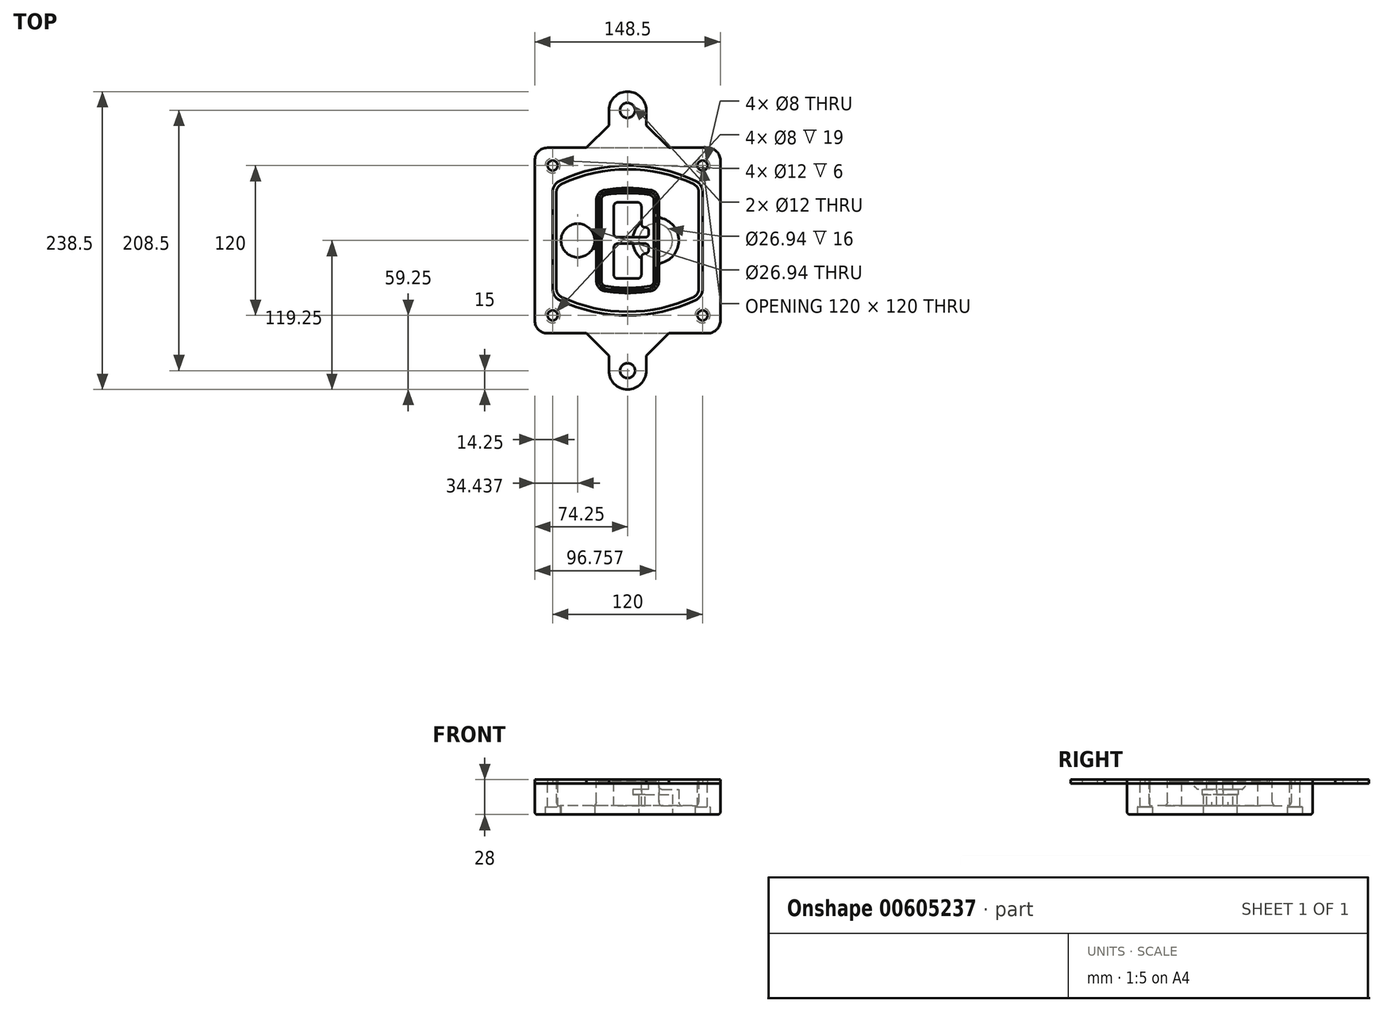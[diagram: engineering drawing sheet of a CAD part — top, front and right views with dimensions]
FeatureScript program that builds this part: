
annotation { "Feature Type Name" : "Feature", "Feature Type Description" : "" }
export const myFeature = defineFeature(function(context is Context, id is Id, definition is map)
    precondition{}
    {
        {
            var Q0;
            Q0=qCreatedBy(makeId("Top.planeOp"),FACE);
            var sketch = newSketch(context, id + "F0", { "sketchPlane" : qUnion([Q0])});
            skPoint(sketch, "E0.rect.middle", {"position": v(0, 0) * mm});
            skLineSegment(sketch, "E1.bottom", {"start": v(-64.25, -74.25) * mm, "end": v(64.25, -74.25) * mm});
            skLineSegment(sketch, "E1.top", {"start": v(-64.25, 74.25) * mm, "end": v(64.25, 74.25) * mm});
            skLineSegment(sketch, "E1.left", {"start": v(-74.25, -64.25) * mm, "end": v(-74.25, 64.25) * mm});
            skLineSegment(sketch, "E1.right", {"start": v(74.25, -64.25) * mm, "end": v(74.25, 64.25) * mm});
            skLineSegment(sketch, "E2", {"start": v(-74.25, 74.25) * mm, "end": v(74.25, -74.25) * mm, "construction": true});
            skLineSegment(sketch, "E3", {"start": v(74.25, 74.25) * mm, "end": v(-74.25, -74.25) * mm, "construction": true});
            skCircle(sketch, "E4", {"center": v(-60, 60) * mm, "radius": 4 * mm});
            skCircle(sketch, "E5", {"center": v(60, 60) * mm, "radius": 4 * mm});
            skCircle(sketch, "E6", {"center": v(60, -60) * mm, "radius": 4 * mm});
            skCircle(sketch, "E7", {"center": v(-60, -60) * mm, "radius": 4 * mm});
            skLineSegment(sketch, "E8", {"start": v(-60, 60) * mm, "end": v(60, 60) * mm, "construction": true});
            skLineSegment(sketch, "E9", {"start": v(60, 60) * mm, "end": v(60, -60) * mm, "construction": true});
            skLineSegment(sketch, "E10", {"start": v(60, -60) * mm, "end": v(-60, -60) * mm, "construction": true});
            skLineSegment(sketch, "E11", {"start": v(-60, -60) * mm, "end": v(-60, 60) * mm, "construction": true});
            skLineSegment(sketch, "E12", {"start": v(-60, 38.83) * mm, "end": v(-60, -38.83) * mm});
            skLineSegment(sketch, "E13", {"start": v(60, 38.83) * mm, "end": v(60, -38.83) * mm});
            skArc(sketch, "E14", {"start": v(54.26, 47.88) * mm, "mid": v(0, 60) * mm, "end": v(-54.26, 47.88) * mm});
            skArc(sketch, "E15", {"start": v(-54.26, -47.88) * mm, "mid": v(0, -60) * mm, "end": v(54.26, -47.88) * mm});
            skLineSegment(sketch, "E16", {"start": v(-60, 0) * mm, "end": v(60, 0) * mm, "construction": true});
            skPoint(sketch, "E17.visualSharp", {"position": v(-60, -45) * mm});
            skArc(sketch, "E17.filletArc", {"start": v(-60, -38.83) * mm, "mid": v(-58.44, -44.2) * mm, "end": v(-54.26, -47.88) * mm});
            skPoint(sketch, "E18.visualSharp", {"position": v(-60, 45) * mm});
            skArc(sketch, "E18.filletArc", {"start": v(-54.26, 47.88) * mm, "mid": v(-58.44, 44.2) * mm, "end": v(-60, 38.83) * mm});
            skPoint(sketch, "E19.visualSharp", {"position": v(60, 45) * mm});
            skArc(sketch, "E19.filletArc", {"start": v(60, 38.83) * mm, "mid": v(58.44, 44.2) * mm, "end": v(54.26, 47.88) * mm});
            skPoint(sketch, "E20.visualSharp", {"position": v(60, -45) * mm});
            skArc(sketch, "E20.filletArc", {"start": v(54.26, -47.88) * mm, "mid": v(58.44, -44.2) * mm, "end": v(60, -38.83) * mm});
            skPoint(sketch, "E21.visualSharp", {"position": v(-74.25, 74.25) * mm});
            skArc(sketch, "E21.filletArc", {"start": v(-64.25, 74.25) * mm, "mid": v(-71.32, 71.32) * mm, "end": v(-74.25, 64.25) * mm});
            skPoint(sketch, "E22.visualSharp", {"position": v(74.25, 74.25) * mm});
            skArc(sketch, "E22.filletArc", {"start": v(74.25, 64.25) * mm, "mid": v(71.32, 71.32) * mm, "end": v(64.25, 74.25) * mm});
            skPoint(sketch, "E23.visualSharp", {"position": v(74.25, -74.25) * mm});
            skArc(sketch, "E23.filletArc", {"start": v(64.25, -74.25) * mm, "mid": v(71.32, -71.32) * mm, "end": v(74.25, -64.25) * mm});
            skPoint(sketch, "E24.visualSharp", {"position": v(-74.25, -74.25) * mm});
            skArc(sketch, "E24.filletArc", {"start": v(-74.25, -64.25) * mm, "mid": v(-71.32, -71.32) * mm, "end": v(-64.25, -74.25) * mm});
            skArc(sketch, "E25.0", {"start": v(57, 38.83) * mm, "mid": v(55.9, 42.58) * mm, "end": v(52.98, 45.17) * mm});
            skLineSegment(sketch, "E25.1", {"start": v(57, 38.83) * mm, "end": v(57, -38.83) * mm});
            skArc(sketch, "E25.2", {"start": v(52.98, -45.17) * mm, "mid": v(55.9, -42.58) * mm, "end": v(57, -38.83) * mm});
            skArc(sketch, "E25.3", {"start": v(-52.98, -45.17) * mm, "mid": v(0, -57) * mm, "end": v(52.98, -45.17) * mm});
            skArc(sketch, "E25.4", {"start": v(-57, -38.83) * mm, "mid": v(-55.9, -42.58) * mm, "end": v(-52.98, -45.17) * mm});
            skArc(sketch, "E25.5", {"start": v(52.98, 45.17) * mm, "mid": v(0, 57) * mm, "end": v(-52.98, 45.17) * mm});
            skLineSegment(sketch, "E25.6", {"start": v(-57, 38.83) * mm, "end": v(-57, -38.83) * mm});
            skArc(sketch, "E25.7", {"start": v(-52.98, 45.17) * mm, "mid": v(-55.9, 42.58) * mm, "end": v(-57, 38.83) * mm});
            skArc(sketch, "E26.0", {"start": v(-55.96, 51.5) * mm, "mid": v(-61.82, 46.33) * mm, "end": v(-64, 38.83) * mm});
            skArc(sketch, "E26.1", {"start": v(55.96, 51.5) * mm, "mid": v(0, 64) * mm, "end": v(-55.96, 51.5) * mm});
            skArc(sketch, "E26.2", {"start": v(64, 38.83) * mm, "mid": v(61.82, 46.33) * mm, "end": v(55.96, 51.5) * mm});
            skLineSegment(sketch, "E26.3", {"start": v(64, 38.83) * mm, "end": v(64, -38.83) * mm});
            skArc(sketch, "E26.4", {"start": v(55.96, -51.5) * mm, "mid": v(61.82, -46.33) * mm, "end": v(64, -38.83) * mm});
            skLineSegment(sketch, "E26.5", {"start": v(-64, 38.83) * mm, "end": v(-64, -38.83) * mm});
            skArc(sketch, "E26.6", {"start": v(-55.96, -51.5) * mm, "mid": v(0, -64) * mm, "end": v(55.96, -51.5) * mm});
            skArc(sketch, "E26.7", {"start": v(-64, -38.83) * mm, "mid": v(-61.82, -46.33) * mm, "end": v(-55.96, -51.5) * mm});
            skSolve(sketch);
        }
        {
            var Q0;
            Q0=makeQuery(id+"F0.imprint","IMPRINT",FACE,{"disambiguationData":[TD([[makeQuery(id+"F0.imprint","IMPRINT",EDGE,{"derivedFrom":sQuery(id+"F0.wireOp",EDGE,"E1.bottom")}),1.0]])]});
            var Q1;
            Q1=makeQuery(id+"F0.imprint","IMPRINT",FACE,{"disambiguationData":[TD([[makeQuery(id+"F0.imprint","IMPRINT",EDGE,{"derivedFrom":sQuery(id+"F0.wireOp",EDGE,"E12")}),1.0]])]});
            var Q2;
            Q2=makeQuery(id+"F0.imprint","IMPRINT",FACE,{"disambiguationData":[TD([[makeQuery(id+"F0.imprint","IMPRINT",EDGE,{"derivedFrom":sQuery(id+"F0.wireOp",EDGE,"E25.0")}),1.0]])]});
            var Q3;
            Q3=makeQuery(id+"F0.imprint","IMPRINT",FACE,{"disambiguationData":[TD([[makeQuery(id+"F0.imprint","IMPRINT",EDGE,{"derivedFrom":sQuery(id+"F0.wireOp",EDGE,"E12")}),-1.0]])]});
            extrude(context, id + "F1", {"entities" : qUnion([Q0, Q1, Q2, Q3]), "oppositeDirection" : true, "depth" : 25 * mm});
        }
        {
            var Q0;
            Q0=makeQuery(id+"F0.imprint","IMPRINT",FACE,{"disambiguationData":[TD([[makeQuery(id+"F0.imprint","IMPRINT",EDGE,{"derivedFrom":sQuery(id+"F0.wireOp",EDGE,"E12")}),1.0]])]});
            extrude(context, id + "F2", {"entities" : qUnion([Q0]), "operationType" : NewBodyOperationType.ADD, "depth" : 3 * mm});
        }
        {
            var Q0;
            Q0=makeQuery(id+"F0.imprint","IMPRINT",FACE,{"disambiguationData":[TD([[makeQuery(id+"F0.imprint","IMPRINT",EDGE,{"derivedFrom":sQuery(id+"F0.wireOp",EDGE,"E25.0")}),1.0]])]});
            extrude(context, id + "F3", {"entities" : qUnion([Q0]), "operationType" : NewBodyOperationType.REMOVE, "oppositeDirection" : true, "depth" : 18 * mm});
        }
        {
            var Q0;
            Q0=makeQuery(id+"F2.opExtrude","CAP_FACE",FACE,{"disambiguationData":[OSD([sQuery(id+"F0.wireOp",EDGE,"E12"),sQuery(id+"F0.wireOp",EDGE,"E13"),sQuery(id+"F0.wireOp",EDGE,"E14"),sQuery(id+"F0.wireOp",EDGE,"E15"),sQuery(id+"F0.wireOp",EDGE,"E17.filletArc"),sQuery(id+"F0.wireOp",EDGE,"E18.filletArc"),sQuery(id+"F0.wireOp",EDGE,"E19.filletArc"),sQuery(id+"F0.wireOp",EDGE,"E20.filletArc"),sQuery(id+"F0.wireOp",EDGE,"E25.0"),sQuery(id+"F0.wireOp",EDGE,"E25.1"),sQuery(id+"F0.wireOp",EDGE,"E25.2"),sQuery(id+"F0.wireOp",EDGE,"E25.3"),sQuery(id+"F0.wireOp",EDGE,"E25.4"),sQuery(id+"F0.wireOp",EDGE,"E25.5"),sQuery(id+"F0.wireOp",EDGE,"E25.6"),sQuery(id+"F0.wireOp",EDGE,"E25.7")])],"isStart":false});
            var sketch = newSketch(context, id + "F4", { "sketchPlane" : qUnion([Q0])});
            skArc(sketch, "E27.0", {"start": v(-18.34, -40.45) * mm, "mid": v(0, -42) * mm, "end": v(18.34, -40.45) * mm});
            skArc(sketch, "E28.0", {"start": v(18.34, 40.45) * mm, "mid": v(0, 42) * mm, "end": v(-18.34, 40.45) * mm});
            skLineSegment(sketch, "E29", {"start": v(-25, 32.57) * mm, "end": v(-25, -32.57) * mm});
            skLineSegment(sketch, "E30", {"start": v(25, 32.57) * mm, "end": v(25, -32.57) * mm});
            skLineSegment(sketch, "E31", {"start": v(-25, 39.1) * mm, "end": v(25, 39.1) * mm, "construction": true});
            skLineSegment(sketch, "E32", {"start": v(-25, -39.1) * mm, "end": v(25, -39.1) * mm, "construction": true});
            skPoint(sketch, "E33.visualSharp", {"position": v(-25, 39.1) * mm});
            skArc(sketch, "E33.filletArc", {"start": v(-18.34, 40.45) * mm, "mid": v(-23.11, 37.73) * mm, "end": v(-25, 32.57) * mm});
            skPoint(sketch, "E34.visualSharp", {"position": v(25, 39.1) * mm});
            skArc(sketch, "E34.filletArc", {"start": v(25, 32.57) * mm, "mid": v(23.11, 37.73) * mm, "end": v(18.34, 40.45) * mm});
            skPoint(sketch, "E35.visualSharp", {"position": v(25, -39.1) * mm});
            skArc(sketch, "E35.filletArc", {"start": v(18.34, -40.45) * mm, "mid": v(23.11, -37.73) * mm, "end": v(25, -32.57) * mm});
            skPoint(sketch, "E36.visualSharp", {"position": v(-25, -39.1) * mm});
            skArc(sketch, "E36.filletArc", {"start": v(-25, -32.57) * mm, "mid": v(-23.11, -37.73) * mm, "end": v(-18.34, -40.45) * mm});
            skArc(sketch, "E37.0", {"start": v(52.98, 45.17) * mm, "mid": v(0, 57) * mm, "end": v(-52.98, 45.17) * mm});
            skArc(sketch, "E37.1", {"start": v(-52.98, 45.17) * mm, "mid": v(-55.9, 42.58) * mm, "end": v(-57, 38.83) * mm});
            skLineSegment(sketch, "E37.2", {"start": v(-57, 38.83) * mm, "end": v(-57, -38.83) * mm});
            skArc(sketch, "E37.3", {"start": v(-57, -38.83) * mm, "mid": v(-55.9, -42.58) * mm, "end": v(-52.98, -45.17) * mm});
            skArc(sketch, "E37.4", {"start": v(-52.98, -45.17) * mm, "mid": v(0, -57) * mm, "end": v(52.98, -45.17) * mm});
            skArc(sketch, "E37.5", {"start": v(52.98, -45.17) * mm, "mid": v(55.9, -42.58) * mm, "end": v(57, -38.83) * mm});
            skLineSegment(sketch, "E37.6", {"start": v(57, 38.83) * mm, "end": v(57, -38.83) * mm});
            skArc(sketch, "E37.7", {"start": v(57, 38.83) * mm, "mid": v(55.9, 42.58) * mm, "end": v(52.98, 45.17) * mm});
            skLineSegment(sketch, "E38.0", {"start": v(23, 32.57) * mm, "end": v(23, -32.57) * mm});
            skArc(sketch, "E38.1", {"start": v(18, -38.48) * mm, "mid": v(21.58, -36.44) * mm, "end": v(23, -32.57) * mm});
            skArc(sketch, "E38.2", {"start": v(-18, -38.48) * mm, "mid": v(0, -40) * mm, "end": v(18, -38.48) * mm});
            skArc(sketch, "E38.3", {"start": v(-23, -32.57) * mm, "mid": v(-21.58, -36.44) * mm, "end": v(-18, -38.48) * mm});
            skLineSegment(sketch, "E38.4", {"start": v(-23, 32.57) * mm, "end": v(-23, -32.57) * mm});
            skArc(sketch, "E38.5", {"start": v(23, 32.57) * mm, "mid": v(21.58, 36.44) * mm, "end": v(18, 38.48) * mm});
            skArc(sketch, "E38.6", {"start": v(-18, 38.48) * mm, "mid": v(-21.58, 36.44) * mm, "end": v(-23, 32.57) * mm});
            skArc(sketch, "E38.7", {"start": v(18, 38.48) * mm, "mid": v(0, 40) * mm, "end": v(-18, 38.48) * mm});
            skArc(sketch, "E39.0", {"start": v(21, 32.57) * mm, "mid": v(20.06, 35.15) * mm, "end": v(17.67, 36.5) * mm});
            skLineSegment(sketch, "E39.1", {"start": v(21, 32.57) * mm, "end": v(21, -32.57) * mm});
            skArc(sketch, "E39.2", {"start": v(17.67, -36.5) * mm, "mid": v(20.06, -35.15) * mm, "end": v(21, -32.57) * mm});
            skArc(sketch, "E39.3", {"start": v(-17.67, -36.5) * mm, "mid": v(0, -38) * mm, "end": v(17.67, -36.5) * mm});
            skArc(sketch, "E39.4", {"start": v(-21, -32.57) * mm, "mid": v(-20.06, -35.15) * mm, "end": v(-17.67, -36.5) * mm});
            skArc(sketch, "E39.5", {"start": v(17.67, 36.5) * mm, "mid": v(0, 38) * mm, "end": v(-17.67, 36.5) * mm});
            skLineSegment(sketch, "E39.6", {"start": v(-21, 32.57) * mm, "end": v(-21, -32.57) * mm});
            skArc(sketch, "E39.7", {"start": v(-17.67, 36.5) * mm, "mid": v(-20.06, 35.15) * mm, "end": v(-21, 32.57) * mm});
            skLineSegment(sketch, "E40", {"start": v(-25, 0) * mm, "end": v(25, 0) * mm, "construction": true});
            skLineSegment(sketch, "E41", {"start": v(-11, 5.5) * mm, "end": v(-11, 27.5) * mm});
            skLineSegment(sketch, "E42", {"start": v(-8, 30.5) * mm, "end": v(8, 30.5) * mm});
            skLineSegment(sketch, "E43", {"start": v(11, 27.5) * mm, "end": v(11, 13.5) * mm});
            skLineSegment(sketch, "E44", {"start": v(14, 10.5) * mm, "end": v(14, 10.5) * mm});
            skLineSegment(sketch, "E45", {"start": v(17, 7.5) * mm, "end": v(17, 5.5) * mm});
            skLineSegment(sketch, "E46", {"start": v(14, 2.5) * mm, "end": v(-8, 2.5) * mm});
            skPoint(sketch, "E47.visualSharp", {"position": v(-11, 30.5) * mm});
            skArc(sketch, "E47.filletArc", {"start": v(-8, 30.5) * mm, "mid": v(-10.12, 29.62) * mm, "end": v(-11, 27.5) * mm});
            skPoint(sketch, "E48.visualSharp", {"position": v(11, 30.5) * mm});
            skArc(sketch, "E48.filletArc", {"start": v(11, 27.5) * mm, "mid": v(10.12, 29.62) * mm, "end": v(8, 30.5) * mm});
            skPoint(sketch, "E49.visualSharp", {"position": v(11, 10.5) * mm});
            skArc(sketch, "E49.filletArc", {"start": v(11, 13.5) * mm, "mid": v(11.88, 11.38) * mm, "end": v(14, 10.5) * mm});
            skPoint(sketch, "E50.visualSharp", {"position": v(17, 10.5) * mm});
            skArc(sketch, "E50.filletArc", {"start": v(17, 7.5) * mm, "mid": v(16.12, 9.62) * mm, "end": v(14, 10.5) * mm});
            skPoint(sketch, "E51.visualSharp", {"position": v(17, 2.5) * mm});
            skArc(sketch, "E51.filletArc", {"start": v(14, 2.5) * mm, "mid": v(16.12, 3.38) * mm, "end": v(17, 5.5) * mm});
            skPoint(sketch, "E52.visualSharp", {"position": v(-11, 2.5) * mm});
            skArc(sketch, "E52.filletArc", {"start": v(-11, 5.5) * mm, "mid": v(-10.12, 3.38) * mm, "end": v(-8, 2.5) * mm});
            skLineSegment(sketch, "E53.0.MirrorCS", {"start": v(14, -2.5) * mm, "end": v(-8, -2.5) * mm});
            skArc(sketch, "E54.0.MirrorCS", {"start": v(-11, -5.5) * mm, "mid": v(-10.12, -3.38) * mm, "end": v(-8, -2.5) * mm});
            skLineSegment(sketch, "E55.0.MirrorCS", {"start": v(-11, -5.5) * mm, "end": v(-11, -27.5) * mm});
            skArc(sketch, "E56.0.MirrorCS", {"start": v(-8, -30.5) * mm, "mid": v(-10.12, -29.62) * mm, "end": v(-11, -27.5) * mm});
            skLineSegment(sketch, "E57.0.MirrorCS", {"start": v(-8, -30.5) * mm, "end": v(8, -30.5) * mm});
            skArc(sketch, "E58.0.MirrorCS", {"start": v(11, -27.5) * mm, "mid": v(10.12, -29.62) * mm, "end": v(8, -30.5) * mm});
            skLineSegment(sketch, "E59.0.MirrorCS", {"start": v(11, -27.5) * mm, "end": v(11, -13.5) * mm});
            skArc(sketch, "E60.0.MirrorCS", {"start": v(11, -13.5) * mm, "mid": v(11.88, -11.38) * mm, "end": v(14, -10.5) * mm});
            skArc(sketch, "E61.0.MirrorCS", {"start": v(17, -7.5) * mm, "mid": v(16.12, -9.62) * mm, "end": v(14, -10.5) * mm});
            skLineSegment(sketch, "E62.0.MirrorCS", {"start": v(17, -7.5) * mm, "end": v(17, -5.5) * mm});
            skArc(sketch, "E63.0.MirrorCS", {"start": v(14, -2.5) * mm, "mid": v(16.12, -3.38) * mm, "end": v(17, -5.5) * mm});
            skSolve(sketch);
        }
        {
            var Q0;
            Q0=makeQuery(id+"F4.imprint","IMPRINT",FACE,{"disambiguationData":[TD([[makeQuery(id+"F4.imprint","IMPRINT",EDGE,{"derivedFrom":sQuery(id+"F4.wireOp",EDGE,"E27.0")}),1.0]])]});
            var Q1;
            Q1=makeQuery(id+"F4.imprint","IMPRINT",FACE,{"disambiguationData":[TD([[makeQuery(id+"F4.imprint","IMPRINT",EDGE,{"derivedFrom":sQuery(id+"F4.wireOp",EDGE,"E38.0")}),-1.0]])]});
            var Q2;
            Q2=makeQuery(id+"F4.imprint","IMPRINT",FACE,{"disambiguationData":[TD([[makeQuery(id+"F4.imprint","IMPRINT",EDGE,{"derivedFrom":sQuery(id+"F4.wireOp",EDGE,"E39.0")}),1.0]])]});
            extrude(context, id + "F5", {"entities" : qUnion([Q0, Q1, Q2]), "operationType" : NewBodyOperationType.ADD, "endBound" : BoundingType.UP_TO_NEXT, "oppositeDirection" : true, "depth" : 25 * mm});
        }
        {
            var Q0;
            Q0=makeQuery(id+"F4.imprint","IMPRINT",FACE,{"disambiguationData":[TD([[makeQuery(id+"F4.imprint","IMPRINT",EDGE,{"derivedFrom":sQuery(id+"F4.wireOp",EDGE,"E38.0")}),-1.0]])]});
            extrude(context, id + "F6", {"entities" : qUnion([Q0]), "operationType" : NewBodyOperationType.REMOVE, "oppositeDirection" : true, "depth" : 2 * mm});
        }
        {
            var Q0;
            Q0=makeQuery(id+"F1.opExtrude","CAP_FACE",FACE,{"disambiguationData":[OSD([sQuery(id+"F0.wireOp",EDGE,"E1.bottom"),sQuery(id+"F0.wireOp",EDGE,"E1.top"),sQuery(id+"F0.wireOp",EDGE,"E1.left"),sQuery(id+"F0.wireOp",EDGE,"E1.right"),sQuery(id+"F0.wireOp",EDGE,"E4"),sQuery(id+"F0.wireOp",EDGE,"E5"),sQuery(id+"F0.wireOp",EDGE,"E6"),sQuery(id+"F0.wireOp",EDGE,"E7"),sQuery(id+"F0.wireOp",EDGE,"E21.filletArc"),sQuery(id+"F0.wireOp",EDGE,"E22.filletArc"),sQuery(id+"F0.wireOp",EDGE,"E23.filletArc"),sQuery(id+"F0.wireOp",EDGE,"E24.filletArc")])],"isStart":false});
            var sketch = newSketch(context, id + "F7", { "sketchPlane" : qUnion([Q0])});
            skCircle(sketch, "E64", {"center": v(22.5, 0) * mm, "radius": 13.47 * mm});
            skCircle(sketch, "E65", {"center": v(-39.81, 0) * mm, "radius": 13.47 * mm});
            skLineSegment(sketch, "E66", {"start": v(74.25, 0) * mm, "end": v(-74.25, 0) * mm});
            skCircle(sketch, "E67", {"center": v(22.5, 0) * mm, "radius": 18.47 * mm});
            skCircle(sketch, "E68", {"center": v(60, -60) * mm, "radius": 6 * mm});
            skCircle(sketch, "E69", {"center": v(-60, -60) * mm, "radius": 6 * mm});
            skCircle(sketch, "E70", {"center": v(-60, 60) * mm, "radius": 6 * mm});
            skCircle(sketch, "E71", {"center": v(60, 60) * mm, "radius": 6 * mm});
            skSolve(sketch);
        }
        {
            var Q0;
            {var subQ1=sQuery(id+"F7.wireOp",EDGE,"E66");var subQ4=sQuery(id+"F7.wireOp",EDGE,"E64");var subQ6=makeQuery(id+"F7.imprint","INTERSECT",VERTEX,{"disambiguationData":[OD(0.0)],"derivedFrom":[subQ4,subQ1]});Q0=makeQuery(id+"F7.imprint","IMPRINT",FACE,{"disambiguationData":[TD([[makeQuery(id+"F7.imprint","IMPRINT",EDGE,{"disambiguationData":[TD([[subQ6,-1.0]])],"derivedFrom":subQ4}),-1.0]])]});}
            var Q1;
            {var subQ0=sQuery(id+"F7.wireOp",EDGE,"E66");var subQ1=sQuery(id+"F7.wireOp",EDGE,"E64");var subQ3=makeQuery(id+"F7.imprint","INTERSECT",VERTEX,{"disambiguationData":[OD(0.0)],"derivedFrom":[subQ1,subQ0]});Q1=makeQuery(id+"F7.imprint","IMPRINT",FACE,{"disambiguationData":[TD([[makeQuery(id+"F7.imprint","IMPRINT",EDGE,{"disambiguationData":[TD([[subQ3,-1.0]])],"derivedFrom":subQ1}),1.0]])]});}
            var Q2;
            {var subQ0=sQuery(id+"F7.wireOp",EDGE,"E66");var subQ1=sQuery(id+"F7.wireOp",EDGE,"E64");var subQ3=makeQuery(id+"F7.imprint","INTERSECT",VERTEX,{"disambiguationData":[OD(0.0)],"derivedFrom":[subQ1,subQ0]});Q2=makeQuery(id+"F7.imprint","IMPRINT",FACE,{"disambiguationData":[TD([[makeQuery(id+"F7.imprint","IMPRINT",EDGE,{"disambiguationData":[TD([[subQ3,1.0]])],"derivedFrom":subQ1}),1.0]])]});}
            var Q3;
            {var subQ1=sQuery(id+"F7.wireOp",EDGE,"E66");var subQ4=sQuery(id+"F7.wireOp",EDGE,"E64");var subQ6=makeQuery(id+"F7.imprint","INTERSECT",VERTEX,{"disambiguationData":[OD(0.0)],"derivedFrom":[subQ4,subQ1]});Q3=makeQuery(id+"F7.imprint","IMPRINT",FACE,{"disambiguationData":[TD([[makeQuery(id+"F7.imprint","IMPRINT",EDGE,{"disambiguationData":[TD([[subQ6,1.0]])],"derivedFrom":subQ4}),-1.0]])]});}
            extrude(context, id + "F8", {"entities" : qUnion([Q0, Q1, Q2, Q3]), "operationType" : NewBodyOperationType.ADD, "oppositeDirection" : true, "depth" : 20 * mm});
        }
        {
            var Q0;
            {var subQ0=sQuery(id+"F7.wireOp",EDGE,"E66");var subQ1=sQuery(id+"F7.wireOp",EDGE,"E64");var subQ3=makeQuery(id+"F7.imprint","INTERSECT",VERTEX,{"disambiguationData":[OD(0.0)],"derivedFrom":[subQ1,subQ0]});Q0=makeQuery(id+"F7.imprint","IMPRINT",FACE,{"disambiguationData":[TD([[makeQuery(id+"F7.imprint","IMPRINT",EDGE,{"disambiguationData":[TD([[subQ3,-1.0]])],"derivedFrom":subQ1}),1.0]])]});}
            var Q1;
            {var subQ0=sQuery(id+"F7.wireOp",EDGE,"E66");var subQ1=sQuery(id+"F7.wireOp",EDGE,"E64");var subQ3=makeQuery(id+"F7.imprint","INTERSECT",VERTEX,{"disambiguationData":[OD(0.0)],"derivedFrom":[subQ1,subQ0]});Q1=makeQuery(id+"F7.imprint","IMPRINT",FACE,{"disambiguationData":[TD([[makeQuery(id+"F7.imprint","IMPRINT",EDGE,{"disambiguationData":[TD([[subQ3,1.0]])],"derivedFrom":subQ1}),1.0]])]});}
            extrude(context, id + "F9", {"entities" : qUnion([Q0, Q1]), "operationType" : NewBodyOperationType.REMOVE, "oppositeDirection" : true, "depth" : 16 * mm});
        }
        {
            var Q0;
            {var subQ0=sQuery(id+"F7.wireOp",EDGE,"E66");var subQ1=sQuery(id+"F7.wireOp",EDGE,"E65");var subQ3=makeQuery(id+"F7.imprint","INTERSECT",VERTEX,{"disambiguationData":[OD(0.0)],"derivedFrom":[subQ1,subQ0]});Q0=makeQuery(id+"F7.imprint","IMPRINT",FACE,{"disambiguationData":[TD([[makeQuery(id+"F7.imprint","IMPRINT",EDGE,{"disambiguationData":[TD([[subQ3,-1.0]])],"derivedFrom":subQ1}),1.0]])]});}
            var Q1;
            {var subQ0=sQuery(id+"F7.wireOp",EDGE,"E66");var subQ1=sQuery(id+"F7.wireOp",EDGE,"E65");var subQ3=makeQuery(id+"F7.imprint","INTERSECT",VERTEX,{"disambiguationData":[OD(0.0)],"derivedFrom":[subQ1,subQ0]});Q1=makeQuery(id+"F7.imprint","IMPRINT",FACE,{"disambiguationData":[TD([[makeQuery(id+"F7.imprint","IMPRINT",EDGE,{"disambiguationData":[TD([[subQ3,1.0]])],"derivedFrom":subQ1}),1.0]])]});}
            extrude(context, id + "F10", {"entities" : qUnion([Q0, Q1]), "operationType" : NewBodyOperationType.REMOVE, "oppositeDirection" : true, "depth" : 25 * mm});
        }
        {
            var Q0;
            Q0=makeQuery(id+"F7.imprint","IMPRINT",FACE,{"disambiguationData":[TD([[makeQuery(id+"F7.imprint","IMPRINT",EDGE,{"derivedFrom":sQuery(id+"F7.wireOp",EDGE,"E68")}),1.0]])]});
            var Q1;
            Q1=makeQuery(id+"F7.imprint","IMPRINT",FACE,{"disambiguationData":[TD([[makeQuery(id+"F7.imprint","IMPRINT",EDGE,{"derivedFrom":makeQuery(id+"F1.opExtrude","CAP_EDGE",EDGE,{"disambiguationData":[OSD([sQuery(id+"F0.wireOp",EDGE,"E5")])],"isStart":false})}),-1.0]])]});
            var Q2;
            Q2=makeQuery(id+"F7.imprint","IMPRINT",FACE,{"disambiguationData":[TD([[makeQuery(id+"F7.imprint","IMPRINT",EDGE,{"derivedFrom":sQuery(id+"F7.wireOp",EDGE,"E69")}),1.0]])]});
            var Q3;
            Q3=makeQuery(id+"F7.imprint","IMPRINT",FACE,{"disambiguationData":[TD([[makeQuery(id+"F7.imprint","IMPRINT",EDGE,{"derivedFrom":makeQuery(id+"F1.opExtrude","CAP_EDGE",EDGE,{"disambiguationData":[OSD([sQuery(id+"F0.wireOp",EDGE,"E4")])],"isStart":false})}),-1.0]])]});
            var Q4;
            Q4=makeQuery(id+"F7.imprint","IMPRINT",FACE,{"disambiguationData":[TD([[makeQuery(id+"F7.imprint","IMPRINT",EDGE,{"derivedFrom":sQuery(id+"F7.wireOp",EDGE,"E70")}),1.0]])]});
            var Q5;
            Q5=makeQuery(id+"F7.imprint","IMPRINT",FACE,{"disambiguationData":[TD([[makeQuery(id+"F7.imprint","IMPRINT",EDGE,{"derivedFrom":makeQuery(id+"F1.opExtrude","CAP_EDGE",EDGE,{"disambiguationData":[OSD([sQuery(id+"F0.wireOp",EDGE,"E7")])],"isStart":false})}),-1.0]])]});
            var Q6;
            Q6=makeQuery(id+"F7.imprint","IMPRINT",FACE,{"disambiguationData":[TD([[makeQuery(id+"F7.imprint","IMPRINT",EDGE,{"derivedFrom":sQuery(id+"F7.wireOp",EDGE,"E71")}),1.0]])]});
            var Q7;
            Q7=makeQuery(id+"F7.imprint","IMPRINT",FACE,{"disambiguationData":[TD([[makeQuery(id+"F7.imprint","IMPRINT",EDGE,{"derivedFrom":makeQuery(id+"F1.opExtrude","CAP_EDGE",EDGE,{"disambiguationData":[OSD([sQuery(id+"F0.wireOp",EDGE,"E6")])],"isStart":false})}),-1.0]])]});
            extrude(context, id + "F11", {"entities" : qUnion([Q0, Q1, Q2, Q3, Q4, Q5, Q6, Q7]), "operationType" : NewBodyOperationType.REMOVE, "oppositeDirection" : true, "depth" : 6 * mm});
        }
        {
            var Q0;
            Q0=makeQuery(id+"F9.boolean.opBoolean","COPY",FACE,{"derivedFrom":makeQuery(id+"F9.opExtrude","CAP_FACE",FACE,{"disambiguationData":[OSD([sQuery(id+"F7.wireOp",EDGE,"E64")])],"isStart":false})});
            var sketch = newSketch(context, id + "F12", { "sketchPlane" : qUnion([Q0])});
            skArc(sketch, "E72.0", {"start": v(11, 14.45) * mm, "mid": v(6.45, 9.13) * mm, "end": v(4.2, 2.5) * mm});
            skArc(sketch, "E72.1", {"start": v(4.2, -2.5) * mm, "mid": v(6.45, -9.13) * mm, "end": v(11, -14.45) * mm});
            skLineSegment(sketch, "E73", {"start": v(4.2, -2.5) * mm, "end": v(14, -2.5) * mm});
            skLineSegment(sketch, "E74.0", {"start": v(14, 2.5) * mm, "end": v(4.2, 2.5) * mm});
            skArc(sketch, "E74.1", {"start": v(14, 2.5) * mm, "mid": v(16.12, 3.38) * mm, "end": v(17, 5.5) * mm});
            skLineSegment(sketch, "E74.2", {"start": v(17, 7.5) * mm, "end": v(17, 5.5) * mm});
            skArc(sketch, "E74.3", {"start": v(17, 7.5) * mm, "mid": v(16.12, 9.62) * mm, "end": v(14, 10.5) * mm});
            skArc(sketch, "E74.4", {"start": v(11, 13.5) * mm, "mid": v(11.88, 11.38) * mm, "end": v(14, 10.5) * mm});
            skLineSegment(sketch, "E74.5", {"start": v(11, 14.45) * mm, "end": v(11, 13.5) * mm});
            skLineSegment(sketch, "E74.7", {"start": v(14, -2.5) * mm, "end": v(4.2, -2.5) * mm});
            skArc(sketch, "E74.8", {"start": v(14, -2.5) * mm, "mid": v(16.12, -3.38) * mm, "end": v(17, -5.5) * mm});
            skLineSegment(sketch, "E74.9", {"start": v(17, -7.5) * mm, "end": v(17, -5.5) * mm});
            skArc(sketch, "E74.10", {"start": v(17, -7.5) * mm, "mid": v(16.12, -9.62) * mm, "end": v(14, -10.5) * mm});
            skArc(sketch, "E74.11", {"start": v(11, -13.5) * mm, "mid": v(11.88, -11.38) * mm, "end": v(14, -10.5) * mm});
            skLineSegment(sketch, "E74.12", {"start": v(11, -14.45) * mm, "end": v(11, -13.5) * mm});
            skPoint(sketch, "E75.orphan", {"position": v(11, -27.5) * mm});
            skPoint(sketch, "E76.orphan", {"position": v(-8, -2.5) * mm});
            skPoint(sketch, "E77.orphan", {"position": v(-8, 2.5) * mm});
            skPoint(sketch, "E78.orphan", {"position": v(11, 27.5) * mm});
            skSolve(sketch);
        }
        {
            var Q0;
            {var subQ7=sQuery(id+"F12.wireOp",EDGE,"E72.0");var subQ14=sQuery(id+"F12.wireOp",EDGE,"E72.1");var subQ16=sQuery(id+"F12.wireOp",EDGE,"E74.1");var subQ18=sQuery(id+"F12.wireOp",EDGE,"E74.8");Q0=qUnion([makeQuery(id+"F12.imprint","IMPRINT",FACE,{"disambiguationData":[TD([[makeQuery(id+"F12.imprint","IMPRINT",EDGE,{"derivedFrom":subQ7}),1.0]])]}),makeQuery(id+"F12.imprint","IMPRINT",FACE,{"disambiguationData":[TD([[makeQuery(id+"F12.imprint","IMPRINT",EDGE,{"derivedFrom":subQ14}),1.0]])]}),makeQuery(id+"F12.imprint","IMPRINT",FACE,{"disambiguationData":[TD([[makeQuery(id+"F12.imprint","IMPRINT",EDGE,{"derivedFrom":subQ16}),1.0]])]}),makeQuery(id+"F12.imprint","IMPRINT",FACE,{"disambiguationData":[TD([[makeQuery(id+"F12.imprint","IMPRINT",EDGE,{"derivedFrom":subQ18}),-1.0]])]})]);}
            var Q1;
            Q1=makeQuery(id+"F5.boolean.opBoolean","SPLIT",FACE,{"disambiguationData":[TD([makeQuery(id+"F5.opExtrude","SWEPT_FACE",FACE,{"disambiguationData":[OSD([sQuery(id+"F4.wireOp",EDGE,"E41")])]})])],"derivedFrom":makeQuery(id+"F3.boolean.opBoolean","COPY",FACE,{"derivedFrom":makeQuery(id+"F3.opExtrude","CAP_FACE",FACE,{"disambiguationData":[OSD([sQuery(id+"F0.wireOp",EDGE,"E25.0"),sQuery(id+"F0.wireOp",EDGE,"E25.1"),sQuery(id+"F0.wireOp",EDGE,"E25.2"),sQuery(id+"F0.wireOp",EDGE,"E25.3"),sQuery(id+"F0.wireOp",EDGE,"E25.4"),sQuery(id+"F0.wireOp",EDGE,"E25.5"),sQuery(id+"F0.wireOp",EDGE,"E25.6"),sQuery(id+"F0.wireOp",EDGE,"E25.7")])],"isStart":false})})});
            extrude(context, id + "F13", {"entities" : qUnion([Q0]), "operationType" : NewBodyOperationType.REMOVE, "endBound" : BoundingType.UP_TO_SURFACE, "endBoundEntityFace" : qUnion([Q1]), "depth" : 25 * mm});
        }
        {
            var Q0;
            Q0=makeQuery(id+"F3.boolean.opBoolean","COPY",EDGE,{"derivedFrom":makeQuery(id+"F3.opExtrude","CAP_EDGE",EDGE,{"disambiguationData":[OSD([sQuery(id+"F0.wireOp",EDGE,"E25.6")])],"isStart":false})});
            var Q1;
            Q1=makeQuery(id+"F8.boolean.opBoolean","INTERSECT",EDGE,{"derivedFrom":[makeQuery(id+"F5.opExtrude","SWEPT_FACE",FACE,{"disambiguationData":[OSD([sQuery(id+"F4.wireOp",EDGE,"E30")])]}),makeQuery(id+"F8.opExtrude","CAP_FACE",FACE,{"disambiguationData":[OSD([sQuery(id+"F7.wireOp",EDGE,"E67")])],"isStart":false})]});
            var Q2;
            Q2=makeQuery(id+"F8.boolean.opBoolean","INTERSECT",EDGE,{"disambiguationData":[OD(1.0)],"derivedFrom":[makeQuery(id+"F5.opExtrude","SWEPT_FACE",FACE,{"disambiguationData":[OSD([sQuery(id+"F4.wireOp",EDGE,"E30")])]}),makeQuery(id+"F8.opExtrude","SWEPT_FACE",FACE,{"disambiguationData":[OSD([sQuery(id+"F7.wireOp",EDGE,"E67")])]})]});
            var Q3;
            {var subQ0=sQuery(id+"F4.wireOp",EDGE,"E30");Q3=makeQuery(id+"F8.boolean.opBoolean","SPLIT",EDGE,{"disambiguationData":[TD([makeQuery(id+"F5.opExtrude","SWEPT_FACE",FACE,{"disambiguationData":[OSD([sQuery(id+"F4.wireOp",EDGE,"E35.filletArc")])]})])],"derivedFrom":makeQuery(id+"F5.opExtrude","CAP_EDGE",EDGE,{"disambiguationData":[OSD([subQ0])],"isStart":false})});}
            var Q4;
            {var subQ0=sQuery(id+"F0.wireOp",EDGE,"E25.7");var subQ1=sQuery(id+"F0.wireOp",EDGE,"E25.1");var subQ2=sQuery(id+"F0.wireOp",EDGE,"E25.6");var subQ3=sQuery(id+"F0.wireOp",EDGE,"E25.5");var subQ4=sQuery(id+"F0.wireOp",EDGE,"E25.4");var subQ5=sQuery(id+"F0.wireOp",EDGE,"E25.0");var subQ6=sQuery(id+"F0.wireOp",EDGE,"E25.2");var subQ7=sQuery(id+"F0.wireOp",EDGE,"E25.3");Q4=makeQuery(id+"F8.boolean.opBoolean","INTERSECT",EDGE,{"derivedFrom":[makeQuery(id+"F5.boolean.opBoolean","SPLIT",FACE,{"disambiguationData":[TD([makeQuery(id+"F2.opExtrude","SWEPT_FACE",FACE,{"disambiguationData":[OSD([subQ5])]})])],"derivedFrom":makeQuery(id+"F3.boolean.opBoolean","COPY",FACE,{"derivedFrom":makeQuery(id+"F3.opExtrude","CAP_FACE",FACE,{"disambiguationData":[OSD([subQ5,subQ1,subQ6,subQ7,subQ4,subQ3,subQ2,subQ0])],"isStart":false})})}),makeQuery(id+"F8.opExtrude","SWEPT_FACE",FACE,{"disambiguationData":[OSD([sQuery(id+"F7.wireOp",EDGE,"E67")])]})]});}
            var Q5;
            Q5=makeQuery(id+"F8.boolean.opBoolean","INTERSECT",EDGE,{"disambiguationData":[OD(0.0)],"derivedFrom":[makeQuery(id+"F5.opExtrude","SWEPT_FACE",FACE,{"disambiguationData":[OSD([sQuery(id+"F4.wireOp",EDGE,"E30")])]}),makeQuery(id+"F8.opExtrude","SWEPT_FACE",FACE,{"disambiguationData":[OSD([sQuery(id+"F7.wireOp",EDGE,"E67")])]})]});
            fillet(context, id + "F14", {"entities" : qUnion([Q0, Q1, Q2, Q3, Q4, Q5]), "radius" : 3 * mm, "tangentPropagation" : true, "allowEdgeOverflow" : false});
        }
        {
            var Q0;
            Q0=makeQuery(id+"F1.opExtrude","CAP_EDGE",EDGE,{"disambiguationData":[OSD([sQuery(id+"F0.wireOp",EDGE,"E1.bottom")])],"isStart":false});
            fillet(context, id + "F15", {"entities" : qUnion([Q0]), "radius" : 2 * mm, "tangentPropagation" : true, "allowEdgeOverflow" : false});
        }
        {
            var Q0;
            {var subQ0=sQuery(id+"F0.wireOp",EDGE,"E21.filletArc");var subQ1=sQuery(id+"F0.wireOp",EDGE,"E7");var subQ2=sQuery(id+"F0.wireOp",EDGE,"E6");var subQ3=sQuery(id+"F0.wireOp",EDGE,"E5");var subQ4=sQuery(id+"F0.wireOp",EDGE,"E4");var subQ5=sQuery(id+"F0.wireOp",EDGE,"E22.filletArc");var subQ6=sQuery(id+"F0.wireOp",EDGE,"E1.bottom");var subQ7=sQuery(id+"F0.wireOp",EDGE,"E1.right");var subQ8=sQuery(id+"F0.wireOp",EDGE,"E1.top");var subQ9=sQuery(id+"F0.wireOp",EDGE,"E1.left");var subQ10=sQuery(id+"F0.wireOp",EDGE,"E23.filletArc");var subQ11=sQuery(id+"F0.wireOp",EDGE,"E24.filletArc");Q0=makeQuery(id+"F2.boolean.opBoolean","SPLIT",FACE,{"disambiguationData":[TD([makeQuery(id+"F1.opExtrude","SWEPT_FACE",FACE,{"disambiguationData":[OSD([subQ6])]})])],"derivedFrom":makeQuery(id+"F1.opExtrude","CAP_FACE",FACE,{"disambiguationData":[OSD([subQ6,subQ8,subQ9,subQ7,subQ4,subQ3,subQ2,subQ1,subQ0,subQ5,subQ10,subQ11])],"isStart":true})});}
            var sketch = newSketch(context, id + "F16", { "sketchPlane" : qUnion([Q0])});
            skLineSegment(sketch, "E79.0", {"start": v(-74.25, -64.25) * mm, "end": v(-74.25, 64.25) * mm});
            skArc(sketch, "E80.0", {"start": v(-64.25, 74.25) * mm, "mid": v(-71.32, 71.32) * mm, "end": v(-74.25, 64.25) * mm});
            skLineSegment(sketch, "E81.0", {"start": v(-64.25, 74.25) * mm, "end": v(64.25, 74.25) * mm});
            skArc(sketch, "E82.0", {"start": v(74.25, 64.25) * mm, "mid": v(71.32, 71.32) * mm, "end": v(64.25, 74.25) * mm});
            skLineSegment(sketch, "E83.0", {"start": v(74.25, -64.25) * mm, "end": v(74.25, 64.25) * mm});
            skArc(sketch, "E84.0", {"start": v(64.25, -74.25) * mm, "mid": v(71.32, -71.32) * mm, "end": v(74.25, -64.25) * mm});
            skLineSegment(sketch, "E85.0", {"start": v(-64.25, -74.25) * mm, "end": v(64.25, -74.25) * mm});
            skArc(sketch, "E86.0", {"start": v(-74.25, -64.25) * mm, "mid": v(-71.32, -71.32) * mm, "end": v(-64.25, -74.25) * mm});
            skCircle(sketch, "E87.0", {"center": v(-60, 60) * mm, "radius": 4 * mm});
            skCircle(sketch, "E88.0", {"center": v(-60, -60) * mm, "radius": 4 * mm});
            skCircle(sketch, "E89.0", {"center": v(60, -60) * mm, "radius": 4 * mm});
            skCircle(sketch, "E90.0", {"center": v(60, 60) * mm, "radius": 4 * mm});
            skLineSegment(sketch, "E91.0.0", {"start": v(64.25, 74.25) * mm, "end": v(-64.25, 74.25) * mm});
            skLineSegment(sketch, "E91.0.2", {"start": v(-74.25, 64.25) * mm, "end": v(-74.25, -64.25) * mm});
            skArc(sketch, "E92.0", {"start": v(54.26, 47.88) * mm, "mid": v(0, 60) * mm, "end": v(-54.26, 47.88) * mm});
            skArc(sketch, "E93.0", {"start": v(60, 38.83) * mm, "mid": v(58.44, 44.2) * mm, "end": v(54.26, 47.88) * mm});
            skLineSegment(sketch, "E94.0", {"start": v(60, 38.83) * mm, "end": v(60, -38.83) * mm});
            skArc(sketch, "E95.0", {"start": v(54.26, -47.88) * mm, "mid": v(58.44, -44.2) * mm, "end": v(60, -38.83) * mm});
            skArc(sketch, "E96.0", {"start": v(-54.26, -47.88) * mm, "mid": v(0, -60) * mm, "end": v(54.26, -47.88) * mm});
            skArc(sketch, "E97.0", {"start": v(-60, -38.83) * mm, "mid": v(-58.44, -44.2) * mm, "end": v(-54.26, -47.88) * mm});
            skLineSegment(sketch, "E98.0", {"start": v(-60, 38.83) * mm, "end": v(-60, -38.83) * mm});
            skArc(sketch, "E99.0", {"start": v(-54.26, 47.88) * mm, "mid": v(-58.44, 44.2) * mm, "end": v(-60, 38.83) * mm});
            skLineSegment(sketch, "E100", {"start": v(0, 74.25) * mm, "end": v(0, 104.25) * mm, "construction": true});
            skCircle(sketch, "E101", {"center": v(0, 104.25) * mm, "radius": 6 * mm});
            skArc(sketch, "E102", {"start": v(15, 104.25) * mm, "mid": v(0, 119.25) * mm, "end": v(-15, 104.25) * mm});
            skLineSegment(sketch, "E103", {"start": v(-33, 74.25) * mm, "end": v(-15, 92.25) * mm});
            skLineSegment(sketch, "E104", {"start": v(-15, 92.25) * mm, "end": v(-15, 104.25) * mm});
            skLineSegment(sketch, "E105.MirrorCS", {"start": v(15, 92.25) * mm, "end": v(15, 104.25) * mm});
            skLineSegment(sketch, "E106.MirrorCS", {"start": v(33, 74.25) * mm, "end": v(15, 92.25) * mm});
            skLineSegment(sketch, "E107", {"start": v(0, 0) * mm, "end": v(-115.2, 0) * mm, "construction": true});
            skPoint(sketch, "E107.endSnap0", {"position": v(-60, 0) * mm});
            skLineSegment(sketch, "E108.MirrorCS", {"start": v(33, -74.25) * mm, "end": v(15, -92.25) * mm});
            skLineSegment(sketch, "E109.MirrorCS", {"start": v(15, -92.25) * mm, "end": v(15, -104.25) * mm});
            skLineSegment(sketch, "E110.MirrorCS", {"start": v(0, -74.25) * mm, "end": v(0, -104.25) * mm, "construction": true});
            skArc(sketch, "E111.MirrorCS", {"start": v(15, -104.25) * mm, "mid": v(0, -119.25) * mm, "end": v(-15, -104.25) * mm});
            skLineSegment(sketch, "E112.MirrorCS", {"start": v(-15, -92.25) * mm, "end": v(-15, -104.25) * mm});
            skCircle(sketch, "E113.MirrorC", {"center": v(0, -104.25) * mm, "radius": 6 * mm});
            skLineSegment(sketch, "E114.MirrorCS", {"start": v(-33, -74.25) * mm, "end": v(-15, -92.25) * mm});
            skSolve(sketch);
        }
        {
            var Q0;
            Q0 = qSketchRegion(id + "F16", true);
            var Q1;
            Q1=makeQuery(id+"F2.opExtrude","CAP_FACE",FACE,{"disambiguationData":[OSD([sQuery(id+"F0.wireOp",EDGE,"E12"),sQuery(id+"F0.wireOp",EDGE,"E13"),sQuery(id+"F0.wireOp",EDGE,"E14"),sQuery(id+"F0.wireOp",EDGE,"E15"),sQuery(id+"F0.wireOp",EDGE,"E17.filletArc"),sQuery(id+"F0.wireOp",EDGE,"E18.filletArc"),sQuery(id+"F0.wireOp",EDGE,"E19.filletArc"),sQuery(id+"F0.wireOp",EDGE,"E20.filletArc"),sQuery(id+"F0.wireOp",EDGE,"E25.0"),sQuery(id+"F0.wireOp",EDGE,"E25.1"),sQuery(id+"F0.wireOp",EDGE,"E25.2"),sQuery(id+"F0.wireOp",EDGE,"E25.3"),sQuery(id+"F0.wireOp",EDGE,"E25.4"),sQuery(id+"F0.wireOp",EDGE,"E25.5"),sQuery(id+"F0.wireOp",EDGE,"E25.6"),sQuery(id+"F0.wireOp",EDGE,"E25.7")])],"isStart":false});
            extrude(context, id + "F17", {"entities" : qUnion([Q0]), "endBound" : BoundingType.UP_TO_SURFACE, "depth" : 25 * mm, "endBoundEntityFace" : qUnion([Q1]), "offsetDistance" : 25 * mm});
        }
    });
